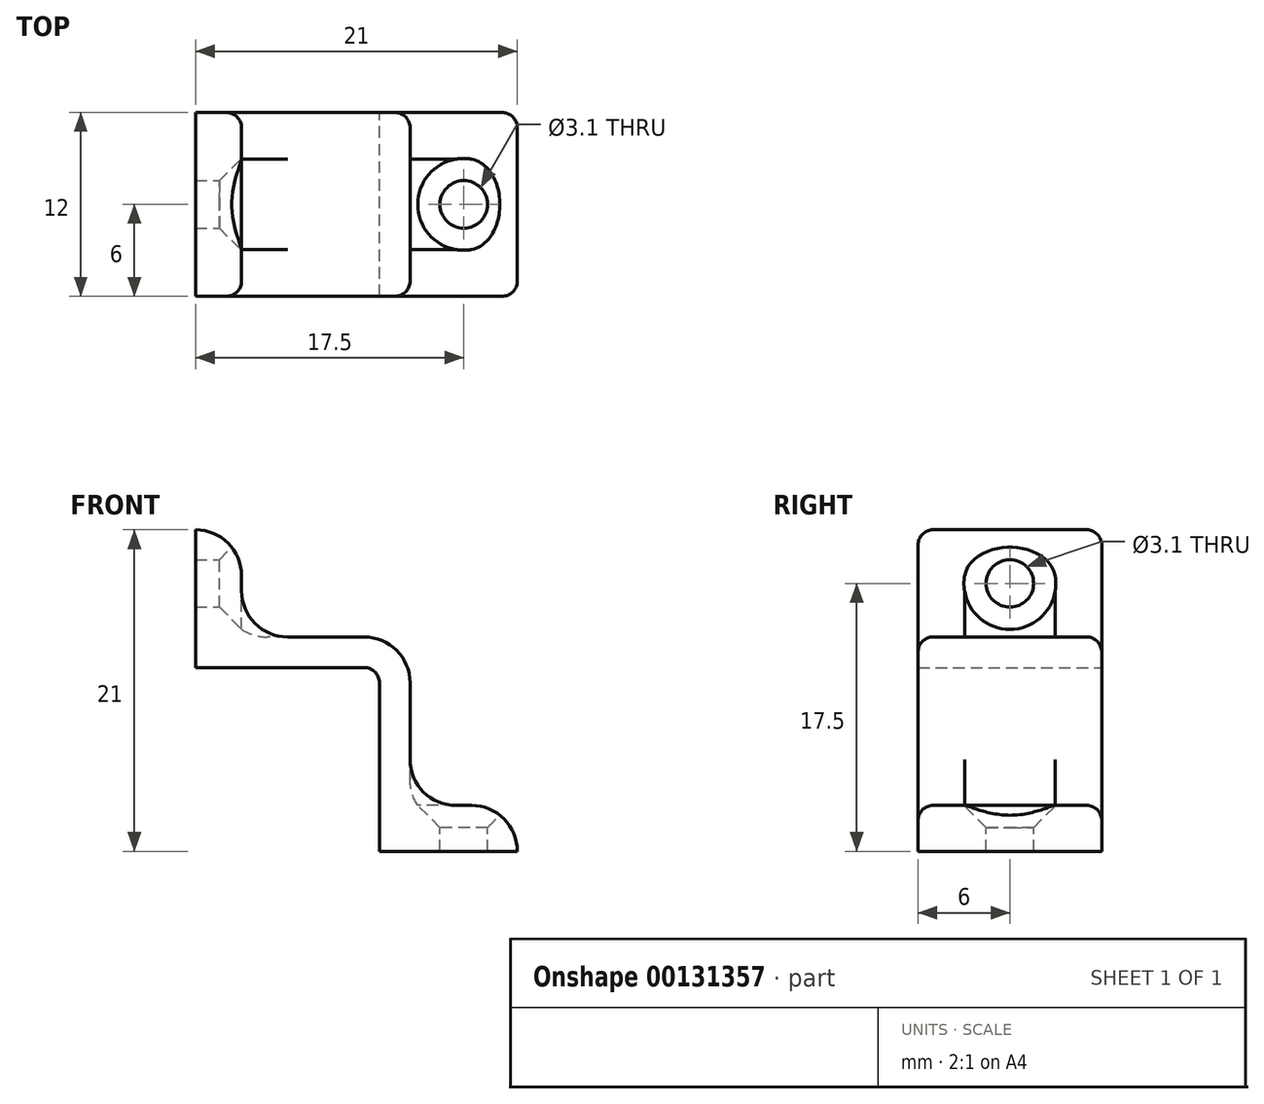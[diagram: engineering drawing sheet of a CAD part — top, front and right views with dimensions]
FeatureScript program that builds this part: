
annotation { "Feature Type Name" : "Feature", "Feature Type Description" : "" }
export const myFeature = defineFeature(function(context is Context, id is Id, definition is map)
    precondition{}
    {
        {
            var Q0;
            Q0=qCreatedBy(makeId("Front.planeOp"),FACE);
            var sketch = newSketch(context, id + "F0", { "sketchPlane" : qUnion([Q0])});
            skLineSegment(sketch, "E0", {"start": v(0, 21) * mm, "end": v(0, 12) * mm});
            skLineSegment(sketch, "E1", {"start": v(0, 12) * mm, "end": v(12, 12) * mm});
            skLineSegment(sketch, "E2", {"start": v(12, 12) * mm, "end": v(12, 0) * mm});
            skLineSegment(sketch, "E3", {"start": v(12, 0) * mm, "end": v(21, 0) * mm});
            skLineSegment(sketch, "E4", {"start": v(21, 0) * mm, "end": v(21, 3) * mm});
            skLineSegment(sketch, "E5", {"start": v(21, 3) * mm, "end": v(14, 3) * mm});
            skLineSegment(sketch, "E6", {"start": v(14, 3) * mm, "end": v(14, 14) * mm});
            skLineSegment(sketch, "E7", {"start": v(14, 14) * mm, "end": v(3, 14) * mm});
            skLineSegment(sketch, "E8", {"start": v(3, 14) * mm, "end": v(3, 21) * mm});
            skLineSegment(sketch, "E9", {"start": v(3, 21) * mm, "end": v(0, 21) * mm});
            skSolve(sketch);
        }
        {
            var Q0;
            Q0 = qSketchRegion(id + "F0", true);
            extrude(context, id + "F1", {"entities" : qUnion([Q0]), "depth" : 12 * mm});
        }
        {
            var Q0;
            Q0=makeQuery(id+"F1.opExtrude","SWEPT_FACE",FACE,{"disambiguationData":[OSD([sQuery(id+"F0.wireOp",EDGE,"E8")])]});
            var sketch = newSketch(context, id + "F2", { "sketchPlane" : qUnion([Q0])});
            skPoint(sketch, "E10", {"position": v(-6, 17.5) * mm});
            skSolve(sketch);
        }
        {
            var Q0;
            Q0=makeQuery(id+"F1.opExtrude","SWEPT_FACE",FACE,{"disambiguationData":[OSD([sQuery(id+"F0.wireOp",EDGE,"E5")])]});
            var sketch = newSketch(context, id + "F3", { "sketchPlane" : qUnion([Q0])});
            skPoint(sketch, "E11", {"position": v(17.5, -6) * mm});
            skSolve(sketch);
        }
        {
            var Q0;
            Q0=sQuery(id+"F2.wireOp",VERTEX,"E10");
            var Q1;
            Q1=sQuery(id+"F3.wireOp",VERTEX,"E11");
            var Q2;
            Q2=makeQuery(id+"F1.opExtrude","SWEPT_BODY",BODY,{"disambiguationData":[OSD([sQuery(id+"F0.wireOp",EDGE,"E0"),sQuery(id+"F0.wireOp",EDGE,"E1"),sQuery(id+"F0.wireOp",EDGE,"E2"),sQuery(id+"F0.wireOp",EDGE,"E3"),sQuery(id+"F0.wireOp",EDGE,"E4"),sQuery(id+"F0.wireOp",EDGE,"E5"),sQuery(id+"F0.wireOp",EDGE,"E6"),sQuery(id+"F0.wireOp",EDGE,"E7"),sQuery(id+"F0.wireOp",EDGE,"E8"),sQuery(id+"F0.wireOp",EDGE,"E9")])]});
            hole(context, id + "F4", {"style" : HoleStyle.C_SINK, "endStyle" : HoleEndStyle.THROUGH, "holeDiameter" : 3.1 * mm, "cSinkDiameter" : 6 * mm, "cSinkAngle" : 90 * degree, "tappedDepth" : 12 * mm, "tapClearance" : 3, "locations" : qUnion([Q0, Q1]), "scope" : qUnion([Q2])});
        }
        {
            var Q0;
            Q0=makeQuery(id+"F1.opExtrude","SWEPT_EDGE",EDGE,{"disambiguationData":[OSD([sQuery(id+"F0.wireOp",EDGE,"E8"),sQuery(id+"F0.wireOp",EDGE,"E9")])]});
            var Q1;
            Q1=makeQuery(id+"F1.opExtrude","SWEPT_EDGE",EDGE,{"disambiguationData":[OSD([sQuery(id+"F0.wireOp",EDGE,"E7"),sQuery(id+"F0.wireOp",EDGE,"E8")])]});
            var Q2;
            Q2=makeQuery(id+"F1.opExtrude","SWEPT_EDGE",EDGE,{"disambiguationData":[OSD([sQuery(id+"F0.wireOp",EDGE,"E6"),sQuery(id+"F0.wireOp",EDGE,"E7")])]});
            var Q3;
            Q3=makeQuery(id+"F1.opExtrude","SWEPT_EDGE",EDGE,{"disambiguationData":[OSD([sQuery(id+"F0.wireOp",EDGE,"E5"),sQuery(id+"F0.wireOp",EDGE,"E6")])]});
            var Q4;
            Q4=makeQuery(id+"F1.opExtrude","SWEPT_EDGE",EDGE,{"disambiguationData":[OSD([sQuery(id+"F0.wireOp",EDGE,"E4"),sQuery(id+"F0.wireOp",EDGE,"E5")])]});
            fillet(context, id + "F5", {"entities" : qUnion([Q0, Q1, Q2, Q3, Q4]), "radius" : 3 * mm, "tangentPropagation" : true, "allowEdgeOverflow" : false});
        }
        {
            var Q0;
            Q0=makeQuery(id+"F1.opExtrude","CAP_EDGE",EDGE,{"disambiguationData":[OSD([sQuery(id+"F0.wireOp",EDGE,"E8")])],"isStart":false});
            var Q1;
            Q1=makeQuery(id+"F1.opExtrude","CAP_EDGE",EDGE,{"disambiguationData":[OSD([sQuery(id+"F0.wireOp",EDGE,"E8")])],"isStart":true});
            var Q2;
            Q2=makeQuery(id+"F1.opExtrude","SWEPT_EDGE",EDGE,{"disambiguationData":[OSD([sQuery(id+"F0.wireOp",EDGE,"E1"),sQuery(id+"F0.wireOp",EDGE,"E2")])]});
            fillet(context, id + "F6", {"entities" : qUnion([Q0, Q1, Q2]), "radius" : 1 * mm, "tangentPropagation" : true, "allowEdgeOverflow" : false});
        }
    });
